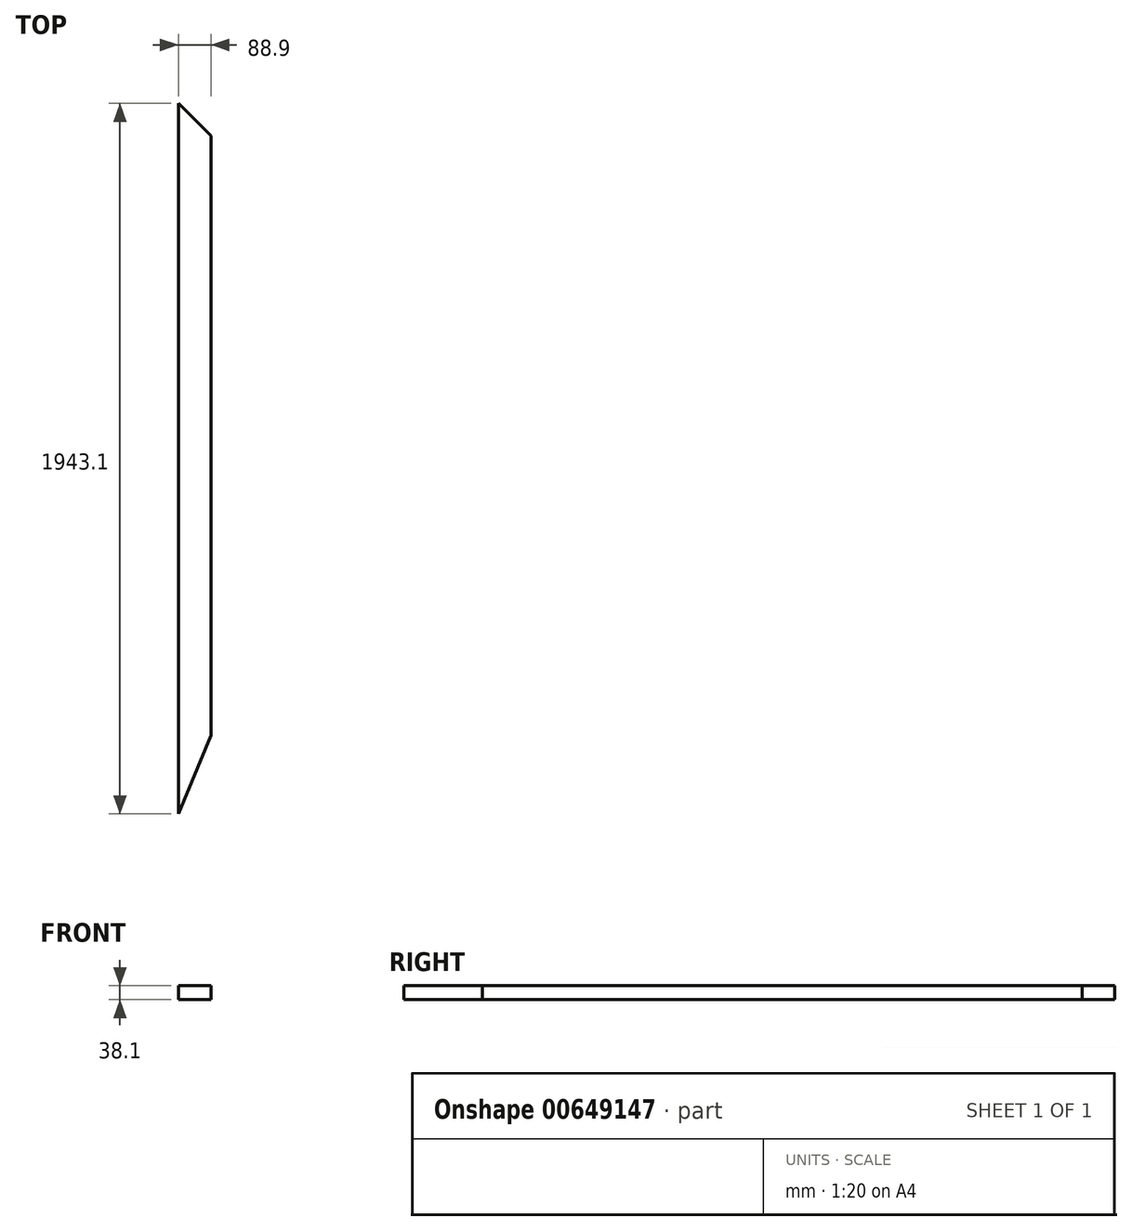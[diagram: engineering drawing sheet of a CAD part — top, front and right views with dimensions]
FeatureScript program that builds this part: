
annotation { "Feature Type Name" : "Feature", "Feature Type Description" : "" }
export const myFeature = defineFeature(function(context is Context, id is Id, definition is map)
    precondition{}
    {
        {
            var Q0;
            Q0=qCreatedBy(makeId("Front.planeOp"),FACE);
            var sketch = newSketch(context, id + "F0", { "sketchPlane" : qUnion([Q0])});
            skLineSegment(sketch, "E0.bottom", {"start": v(0, 0) * mm, "end": v(88.9, 0) * mm});
            skLineSegment(sketch, "E0.top", {"start": v(0, 38.1) * mm, "end": v(88.9, 38.1) * mm});
            skLineSegment(sketch, "E0.left", {"start": v(0, 0) * mm, "end": v(0, 38.1) * mm});
            skLineSegment(sketch, "E0.right", {"start": v(88.9, 0) * mm, "end": v(88.9, 38.1) * mm});
            skSolve(sketch);
        }
        {
            var Q0;
            Q0=qSketchRegion(id+"F0",true);
            extrude(context, id + "F1", {"entities" : qUnion([Q0]), "depth" : 1943.1 * mm, "offsetDistance" : 25.4 * mm});
        }
        {
            var Q0;
            Q0=makeQuery(id+"F1.opExtrude","SWEPT_FACE",FACE,{"disambiguationData":[OSD([sQuery(id+"F0.wireOp",EDGE,"E0.top")])]});
            var sketch = newSketch(context, id + "F2", { "sketchPlane" : qUnion([Q0])});
            skLineSegment(sketch, "E1", {"start": v(0, -1943.1) * mm, "end": v(88.9, -1728.48) * mm});
            skLineSegment(sketch, "E2", {"start": v(88.9, -1728.48) * mm, "end": v(88.9, -1943.1) * mm});
            skLineSegment(sketch, "E3", {"start": v(88.9, -1943.1) * mm, "end": v(0, -1943.1) * mm});
            skSolve(sketch);
        }
        {
            var Q0;
            Q0=qSketchRegion(id+"F2",true);
            extrude(context, id + "F3", {"entities" : qUnion([Q0]), "operationType" : NewBodyOperationType.REMOVE, "endBound" : BoundingType.UP_TO_NEXT, "oppositeDirection" : true, "depth" : 25.4 * mm, "offsetDistance" : 25.4 * mm});
        }
        {
            var Q0;
            Q0=makeQuery(id+"F1.opExtrude","SWEPT_FACE",FACE,{"disambiguationData":[OSD([sQuery(id+"F0.wireOp",EDGE,"E0.top")])]});
            var sketch = newSketch(context, id + "F4", { "sketchPlane" : qUnion([Q0])});
            skLineSegment(sketch, "E4", {"start": v(0, 0) * mm, "end": v(88.9, -88.9) * mm});
            skLineSegment(sketch, "E5", {"start": v(88.9, -88.9) * mm, "end": v(88.9, 0) * mm});
            skLineSegment(sketch, "E6", {"start": v(88.9, 0) * mm, "end": v(0, 0) * mm});
            skSolve(sketch);
        }
        {
            var Q0;
            Q0=makeQuery(id+"F4.imprint","IMPRINT",FACE,{"disambiguationData":[TD([[makeQuery(id+"F4.imprint","IMPRINT",EDGE,{"derivedFrom":sQuery(id+"F4.wireOp",EDGE,"E4")}),1.0]])]});
            extrude(context, id + "F5", {"entities" : qUnion([Q0]), "operationType" : NewBodyOperationType.REMOVE, "endBound" : BoundingType.UP_TO_NEXT, "oppositeDirection" : true, "depth" : 25.4 * mm, "offsetDistance" : 25.4 * mm});
        }
    });
